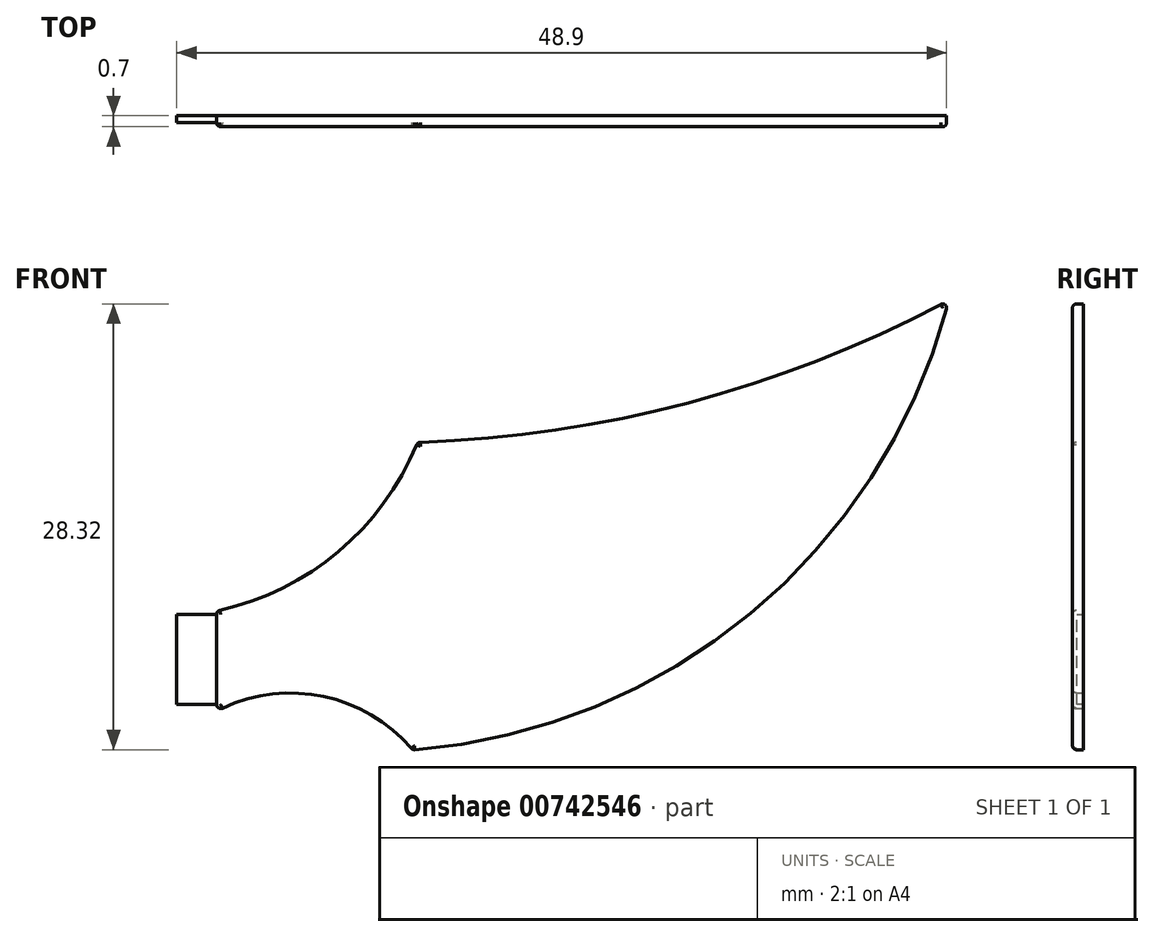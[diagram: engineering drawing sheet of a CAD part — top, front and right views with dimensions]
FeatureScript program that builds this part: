
annotation { "Feature Type Name" : "Feature", "Feature Type Description" : "" }
export const myFeature = defineFeature(function(context is Context, id is Id, definition is map)
    precondition{}
    {
        {
            var Q0;
            Q0=qCreatedBy(makeId("Front.planeOp"),FACE);
            var sketch = newSketch(context, id + "F0", { "sketchPlane" : qUnion([Q0])});
            skLineSegment(sketch, "E0", {"start": v(0, 0) * mm, "end": v(0, 6.35) * mm});
            skLineSegment(sketch, "E1", {"start": v(0, 6.35) * mm, "end": v(12.77, 17.06) * mm, "construction": true});
            skLineSegment(sketch, "E2", {"start": v(12.77, 17.06) * mm, "end": v(46.5, 26.1) * mm, "construction": true});
            skLineSegment(sketch, "E3", {"start": v(12.77, 17.06) * mm, "end": v(12.77, 6.6) * mm, "construction": true});
            skLineSegment(sketch, "E4", {"start": v(46.5, 26.1) * mm, "end": v(12.45, -2.47) * mm, "construction": true});
            skLineSegment(sketch, "E5", {"start": v(46.5, 26.1) * mm, "end": v(46.5, 12.28) * mm, "construction": true});
            skLineSegment(sketch, "E6", {"start": v(0, 0) * mm, "end": v(12.45, -2.47) * mm, "construction": true});
            skArc(sketch, "E7", {"start": v(0, 6.35) * mm, "mid": v(7.72, 10.12) * mm, "end": v(12.77, 17.06) * mm});
            skArc(sketch, "E8", {"start": v(12.77, 17.06) * mm, "mid": v(30.16, 19.63) * mm, "end": v(46.5, 26.1) * mm});
            skArc(sketch, "E9", {"start": v(12.45, -2.47) * mm, "mid": v(34.08, 6.34) * mm, "end": v(46.5, 26.1) * mm});
            skArc(sketch, "E10", {"start": v(12.45, -2.47) * mm, "mid": v(6.66, 0.95) * mm, "end": v(0, 0) * mm});
            skSolve(sketch);
        }
        {
            var Q0;
            Q0=makeQuery(id+"F0.imprint","IMPRINT",FACE,{"disambiguationData":[TD([[makeQuery(id+"F0.imprint","IMPRINT",EDGE,{"derivedFrom":sQuery(id+"F0.wireOp",EDGE,"E0")}),-1.0]])]});
            extrude(context, id + "F1", {"entities" : qUnion([Q0]), "depth" : 1.59 * mm, "offsetDistance" : 25.4 * mm});
        }
        {
            var Q0;
            Q0=makeQuery(id+"F1.opExtrude","CAP_EDGE",EDGE,{"disambiguationData":[OSD([sQuery(id+"F0.wireOp",EDGE,"E7")])],"isStart":true});
            var Q1;
            Q1=makeQuery(id+"F1.opExtrude","CAP_EDGE",EDGE,{"disambiguationData":[OSD([sQuery(id+"F0.wireOp",EDGE,"E7")])],"isStart":false});
            var Q2;
            Q2=makeQuery(id+"F1.opExtrude","CAP_FACE",FACE,{"disambiguationData":[OSD([sQuery(id+"F0.wireOp",EDGE,"E0"),sQuery(id+"F0.wireOp",EDGE,"E7"),sQuery(id+"F0.wireOp",EDGE,"E8"),sQuery(id+"F0.wireOp",EDGE,"E9"),sQuery(id+"F0.wireOp",EDGE,"E10")])],"isStart":true});
            var Q3;
            Q3=makeQuery(id+"F1.opExtrude","CAP_FACE",FACE,{"disambiguationData":[OSD([sQuery(id+"F0.wireOp",EDGE,"E0"),sQuery(id+"F0.wireOp",EDGE,"E7"),sQuery(id+"F0.wireOp",EDGE,"E8"),sQuery(id+"F0.wireOp",EDGE,"E9"),sQuery(id+"F0.wireOp",EDGE,"E10")])],"isStart":false});
            fillet(context, id + "F2", {"entities" : qUnion([Q0, Q1, Q2, Q3]), "radius" : 0.25 * mm, "tangentPropagation" : true, "allowEdgeOverflow" : false});
        }
        {
            var Q0;
            Q0=makeQuery(id+"F1.opExtrude","SWEPT_EDGE",EDGE,{"disambiguationData":[OSD([sQuery(id+"F0.wireOp",EDGE,"E0"),sQuery(id+"F0.wireOp",EDGE,"E7")])]});
            var Q1;
            Q1=makeQuery(id+"F1.opExtrude","SWEPT_EDGE",EDGE,{"disambiguationData":[OSD([sQuery(id+"F0.wireOp",EDGE,"E0"),sQuery(id+"F0.wireOp",EDGE,"E10")])]});
            var Q2;
            Q2=makeQuery(id+"F1.opExtrude","SWEPT_EDGE",EDGE,{"disambiguationData":[OSD([sQuery(id+"F0.wireOp",EDGE,"E9"),sQuery(id+"F0.wireOp",EDGE,"E10")])]});
            var Q3;
            Q3=makeQuery(id+"F1.opExtrude","SWEPT_EDGE",EDGE,{"disambiguationData":[OSD([sQuery(id+"F0.wireOp",EDGE,"E7"),sQuery(id+"F0.wireOp",EDGE,"E8")])]});
            var Q4;
            Q4=makeQuery(id+"F1.opExtrude","SWEPT_EDGE",EDGE,{"disambiguationData":[OSD([sQuery(id+"F0.wireOp",EDGE,"E8"),sQuery(id+"F0.wireOp",EDGE,"E9")])]});
            fillet(context, id + "F3", {"entities" : qUnion([Q0, Q1, Q2, Q3, Q4]), "radius" : 0.25 * mm, "tangentPropagation" : true, "allowEdgeOverflow" : false});
        }
        {
            var Q0;
            Q0=makeQuery(id+"F1.opExtrude","SWEPT_FACE",FACE,{"disambiguationData":[OSD([sQuery(id+"F0.wireOp",EDGE,"E0")])]});
            var sketch = newSketch(context, id + "F4", { "sketchPlane" : qUnion([Q0])});
            skLineSegment(sketch, "E11.bottom", {"start": v(0.25, 6.15) * mm, "end": v(1.33, 6.15) * mm});
            skLineSegment(sketch, "E11.top", {"start": v(0.25, 0.4) * mm, "end": v(1.33, 0.4) * mm});
            skLineSegment(sketch, "E11.left", {"start": v(0.25, 6.15) * mm, "end": v(0.25, 0.4) * mm});
            skLineSegment(sketch, "E11.right", {"start": v(1.33, 6.15) * mm, "end": v(1.33, 0.4) * mm});
            skLineSegment(sketch, "E12.0", {"start": v(0.28, 6.12) * mm, "end": v(0.28, 0.43) * mm});
            skLineSegment(sketch, "E12.1", {"start": v(1.3, 6.12) * mm, "end": v(0.28, 6.12) * mm});
            skLineSegment(sketch, "E12.2", {"start": v(1.3, 0.43) * mm, "end": v(1.3, 6.12) * mm});
            skLineSegment(sketch, "E12.3", {"start": v(0.28, 0.43) * mm, "end": v(1.3, 0.43) * mm});
            skSolve(sketch);
        }
        {
            var Q0;
            Q0=makeQuery(id+"F4.imprint","IMPRINT",FACE,{"disambiguationData":[TD([[makeQuery(id+"F4.imprint","IMPRINT",EDGE,{"derivedFrom":sQuery(id+"F4.wireOp",EDGE,"E12.0")}),1.0]])]});
            extrude(context, id + "F5", {"entities" : qUnion([Q0]), "operationType" : NewBodyOperationType.ADD, "depth" : 2.54 * mm, "offsetDistance" : 25.4 * mm});
        }
        {
            var Q0;
            Q0=qCreatedBy(makeId("Front.planeOp"),FACE);
            cPlane(context, id + "F6", {"entities" : qUnion([Q0]), "cplaneType" : CPlaneType.OFFSET, "offset" : 0.89 * mm, "width" : 152.4 * mm, "height" : 152.4 * mm});
        }
        {
            var Q0;
            Q0=qCreatedBy(id+"F6.planeOp",FACE);
            var sketch = newSketch(context, id + "F7", { "sketchPlane" : qUnion([Q0])});
            skLineSegment(sketch, "E13.bottom", {"start": v(-17.96, 33.87) * mm, "end": v(62.72, 33.87) * mm});
            skLineSegment(sketch, "E13.top", {"start": v(-17.96, -12.9) * mm, "end": v(62.72, -12.9) * mm});
            skLineSegment(sketch, "E13.left", {"start": v(-17.96, 33.87) * mm, "end": v(-17.96, -12.9) * mm});
            skLineSegment(sketch, "E13.right", {"start": v(62.72, 33.87) * mm, "end": v(62.72, -12.9) * mm});
            skSolve(sketch);
        }
        {
            var Q0;
            Q0=makeQuery(id+"F7.imprint","IMPRINT",FACE,{"disambiguationData":[TD([[makeQuery(id+"F7.imprint","IMPRINT",EDGE,{"derivedFrom":sQuery(id+"F7.wireOp",EDGE,"E13.bottom")}),-1.0]])]});
            extrude(context, id + "F8", {"entities" : qUnion([Q0]), "operationType" : NewBodyOperationType.REMOVE, "oppositeDirection" : true, "depth" : 25.4 * mm, "offsetDistance" : 25.4 * mm});
        }
    });
